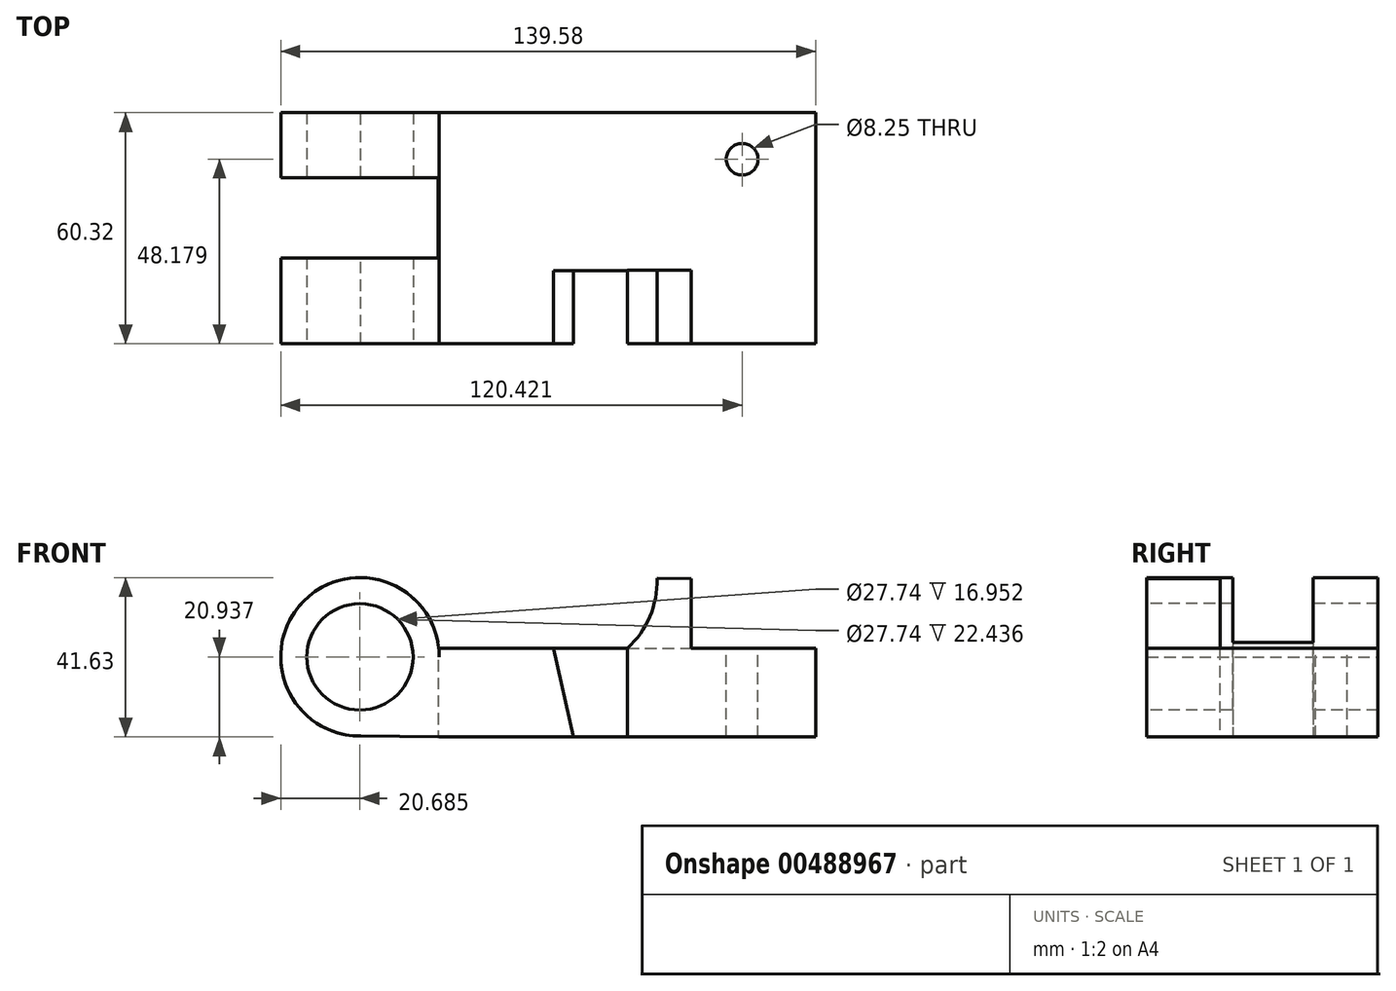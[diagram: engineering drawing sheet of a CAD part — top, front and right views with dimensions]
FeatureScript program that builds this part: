
annotation { "Feature Type Name" : "Feature", "Feature Type Description" : "" }
export const myFeature = defineFeature(function(context is Context, id is Id, definition is map)
    precondition{}
    {
        {
            var Q0;
            Q0=qCreatedBy(makeId("Front.planeOp"),FACE);
            var sketch = newSketch(context, id + "F0", { "sketchPlane" : qUnion([Q0])});
            skLineSegment(sketch, "E0.bottom", {"start": v(-42.5, 0) * mm, "end": v(55.7, 0) * mm});
            skLineSegment(sketch, "E0.top", {"start": v(-42.5, 23.18) * mm, "end": v(55.7, 23.18) * mm});
            skLineSegment(sketch, "E0.left", {"start": v(-42.5, 0) * mm, "end": v(-42.5, 23.18) * mm});
            skLineSegment(sketch, "E0.right", {"start": v(55.7, 0) * mm, "end": v(55.7, 23.18) * mm});
            skCircle(sketch, "E1", {"center": v(-63.19, 20.94) * mm, "radius": 20.69 * mm});
            skLineSegment(sketch, "E2", {"start": v(-63.91, 0.26) * mm, "end": v(-42.5, 0) * mm});
            skLineSegment(sketch, "E3", {"start": v(23.3, 23.18) * mm, "end": v(23.3, 41.38) * mm});
            skLineSegment(sketch, "E4", {"start": v(23.3, 41.38) * mm, "end": v(14.33, 41.4) * mm});
            skArc(sketch, "E5", {"start": v(6.6, 23.18) * mm, "mid": v(12.46, 31.45) * mm, "end": v(14.33, 41.4) * mm});
            skLineSegment(sketch, "E6", {"start": v(6.6, 23.18) * mm, "end": v(6.6, 0) * mm});
            skLineSegment(sketch, "E7", {"start": v(-10.34, 23.18) * mm, "end": v(-3.36, 0) * mm});
            skSolve(sketch);
        }
        {
            var Q0;
            Q0 = qSketchRegion(id + "F0", true);
            extrude(context, id + "F1", {"entities" : qUnion([Q0]), "endBound" : BoundingType.SYMMETRIC, "depth" : 60.32 * mm});
        }
        {
            var Q0;
            Q0=makeQuery(id+"F1.opExtrude","CAP_FACE",FACE,{"disambiguationData":[OSD([sQuery(id+"F0.wireOp",EDGE,"E0.bottom"),sQuery(id+"F0.wireOp",EDGE,"E0.top"),sQuery(id+"F0.wireOp",EDGE,"E0.left"),sQuery(id+"F0.wireOp",EDGE,"E0.right"),sQuery(id+"F0.wireOp",EDGE,"E1"),sQuery(id+"F0.wireOp",EDGE,"E2"),sQuery(id+"F0.wireOp",EDGE,"E3"),sQuery(id+"F0.wireOp",EDGE,"E4"),sQuery(id+"F0.wireOp",EDGE,"E5")])],"isStart":false});
            var sketch = newSketch(context, id + "F2", { "sketchPlane" : qUnion([Q0])});
            skCircle(sketch, "E8", {"center": v(-63.19, 20.94) * mm, "radius": 13.87 * mm});
            skSolve(sketch);
        }
        {
            var Q0;
            Q0=makeQuery(id+"F2.imprint","IMPRINT",FACE,{"disambiguationData":[TD([[makeQuery(id+"F2.imprint","IMPRINT",EDGE,{"derivedFrom":sQuery(id+"F2.wireOp",EDGE,"E8")}),1.0]])]});
            extrude(context, id + "F3", {"entities" : qUnion([Q0]), "operationType" : NewBodyOperationType.REMOVE, "endBound" : BoundingType.SYMMETRIC, "oppositeDirection" : true, "depth" : 254 * mm});
        }
        {
            var Q0;
            Q0=qCreatedBy(makeId("Top.planeOp"),FACE);
            var sketch = newSketch(context, id + "F4", { "sketchPlane" : qUnion([Q0])});
            skLineSegment(sketch, "E9.bottom", {"start": v(-42.84, 13.21) * mm, "end": v(-84.21, 13.21) * mm});
            skLineSegment(sketch, "E9.top", {"start": v(-42.84, -7.73) * mm, "end": v(-84.21, -7.73) * mm});
            skLineSegment(sketch, "E9.left", {"start": v(-42.84, 13.21) * mm, "end": v(-42.84, -7.73) * mm});
            skLineSegment(sketch, "E9.right", {"start": v(-84.21, 13.21) * mm, "end": v(-84.21, -7.73) * mm});
            skSolve(sketch);
        }
        {
            var Q0;
            Q0 = qSketchRegion(id + "F4", true);
            extrude(context, id + "F5", {"entities" : qUnion([Q0]), "operationType" : NewBodyOperationType.REMOVE, "depth" : 46.48 * mm});
        }
        {
            var Q0;
            Q0=makeQuery(id+"F1.opExtrude","CAP_FACE",FACE,{"disambiguationData":[OSD([sQuery(id+"F0.wireOp",EDGE,"E0.bottom"),sQuery(id+"F0.wireOp",EDGE,"E0.top"),sQuery(id+"F0.wireOp",EDGE,"E0.left"),sQuery(id+"F0.wireOp",EDGE,"E0.right"),sQuery(id+"F0.wireOp",EDGE,"E1"),sQuery(id+"F0.wireOp",EDGE,"E2"),sQuery(id+"F0.wireOp",EDGE,"E3"),sQuery(id+"F0.wireOp",EDGE,"E4"),sQuery(id+"F0.wireOp",EDGE,"E5")])],"isStart":false});
            var sketch = newSketch(context, id + "F6", { "sketchPlane" : qUnion([Q0])});
            skLineSegment(sketch, "E10", {"start": v(6.6, 23.18) * mm, "end": v(6.6, 0) * mm});
            skLineSegment(sketch, "E11", {"start": v(-12.68, 23.18) * mm, "end": v(-7.44, 0) * mm});
            skSolve(sketch);
        }
        {
            var Q0;
            {var subQ0=sQuery(id+"F6.wireOp",EDGE,"E10");Q0=makeQuery(id+"F6.imprint","IMPRINT",FACE,{"disambiguationData":[TD([[makeQuery(id+"F6.imprint","IMPRINT",EDGE,{"derivedFrom":subQ0}),-1.0]])]});}
            extrude(context, id + "F7", {"entities" : qUnion([Q0]), "operationType" : NewBodyOperationType.REMOVE, "oppositeDirection" : true, "depth" : 19.05 * mm});
        }
        {
            var Q0;
            {var subQ0=sQuery(id+"F0.wireOp",EDGE,"E0.top");Q0=makeQuery(id+"F1.opExtrude","SWEPT_FACE",FACE,{"disambiguationData":[OSD([subQ0]),TDD([makeQuery(id+"F0.imprint","IMPRINT",EDGE,{"disambiguationData":[TD([[makeQuery(id+"F0.imprint","INTERSECT",VERTEX,{"derivedFrom":[subQ0,sQuery(id+"F0.wireOp",EDGE,"E0.right")]}),1.0]])],"derivedFrom":subQ0})])]});}
            var sketch = newSketch(context, id + "F8", { "sketchPlane" : qUnion([Q0])});
            skCircle(sketch, "E12", {"center": v(36.55, 18.02) * mm, "radius": 4.13 * mm});
            skLineSegment(sketch, "E13.bottom", {"start": v(6.26, 30.16) * mm, "end": v(23.3, 30.16) * mm});
            skLineSegment(sketch, "E13.top", {"start": v(6.26, -10.97) * mm, "end": v(23.3, -10.97) * mm});
            skLineSegment(sketch, "E13.left", {"start": v(6.26, 30.16) * mm, "end": v(6.26, -10.97) * mm});
            skLineSegment(sketch, "E13.right", {"start": v(23.3, 30.16) * mm, "end": v(23.3, -10.97) * mm});
            skSolve(sketch);
        }
        {
            var Q0;
            Q0=makeQuery(id+"F8.imprint","IMPRINT",FACE,{"disambiguationData":[TD([[makeQuery(id+"F8.imprint","IMPRINT",EDGE,{"derivedFrom":sQuery(id+"F8.wireOp",EDGE,"E13.bottom")}),-1.0]])]});
            extrude(context, id + "F9", {"entities" : qUnion([Q0]), "operationType" : NewBodyOperationType.REMOVE, "depth" : 26.16 * mm});
        }
        {
            var Q0;
            Q0=makeQuery(id+"F8.imprint","IMPRINT",FACE,{"disambiguationData":[TD([[makeQuery(id+"F8.imprint","IMPRINT",EDGE,{"derivedFrom":sQuery(id+"F8.wireOp",EDGE,"E12")}),1.0]])]});
            extrude(context, id + "F10", {"entities" : qUnion([Q0]), "operationType" : NewBodyOperationType.REMOVE, "oppositeDirection" : true, "depth" : 48 * mm});
        }
    });
